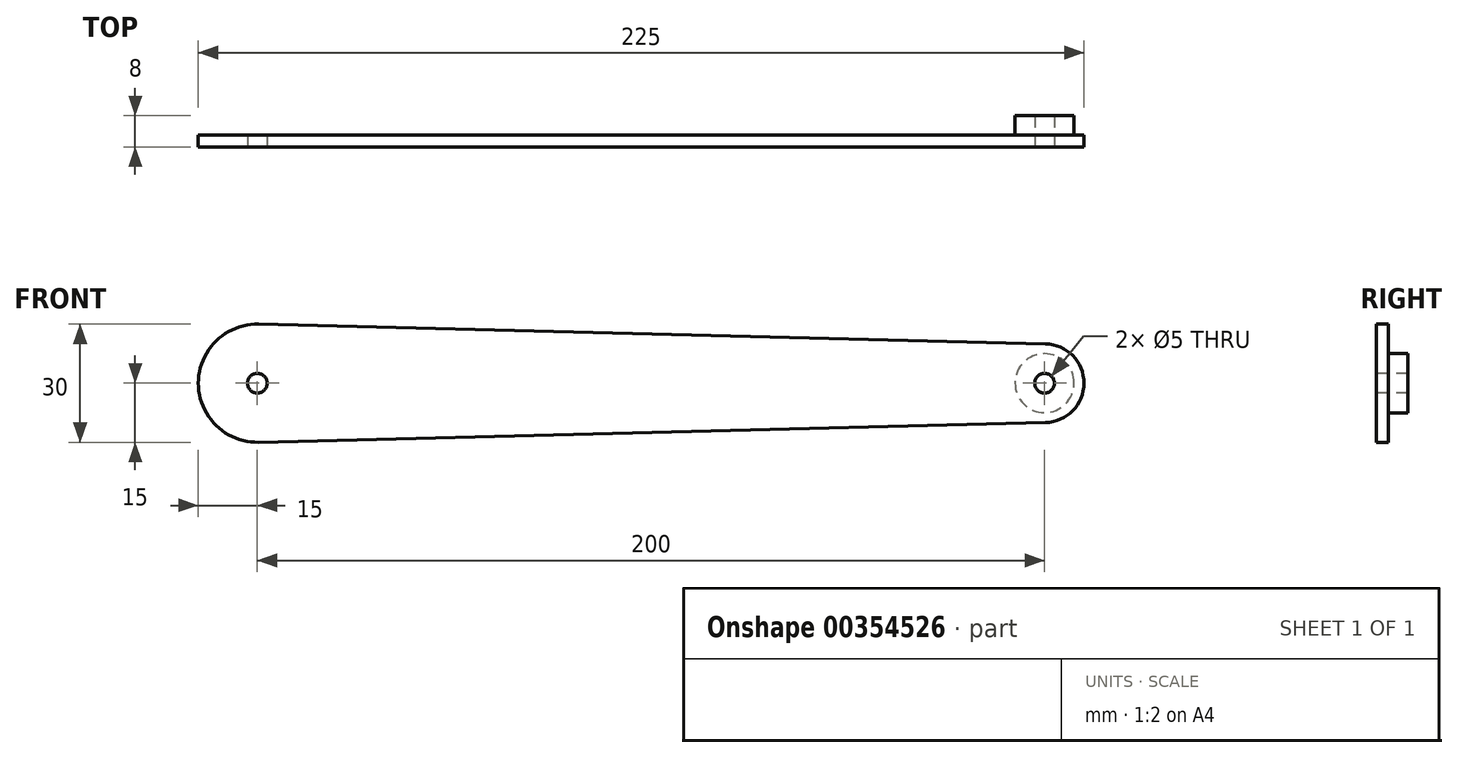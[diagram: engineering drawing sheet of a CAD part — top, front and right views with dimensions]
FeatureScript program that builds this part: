
annotation { "Feature Type Name" : "Feature", "Feature Type Description" : "" }
export const myFeature = defineFeature(function(context is Context, id is Id, definition is map)
    precondition{}
    {
        {
            var Q0;
            Q0=qCreatedBy(makeId("Front.planeOp"),FACE);
            var sketch = newSketch(context, id + "F0", { "sketchPlane" : qUnion([Q0])});
            skArc(sketch, "E0", {"start": v(0.38, 15) * mm, "mid": v(-15, 0) * mm, "end": v(0.37, -15) * mm});
            skArc(sketch, "E1", {"start": v(200.25, 10) * mm, "mid": v(210, 0) * mm, "end": v(200.25, -10) * mm});
            skLineSegment(sketch, "E2", {"start": v(0.37, 15) * mm, "end": v(200.25, 10) * mm});
            skLineSegment(sketch, "E3", {"start": v(200.25, -10) * mm, "end": v(0.37, -15) * mm});
            skCircle(sketch, "E4", {"center": v(200, 0) * mm, "radius": 2.5 * mm});
            skSolve(sketch);
        }
        {
            var Q0;
            Q0 = qSketchRegion(id + "F0", true);
            extrude(context, id + "F1", {"entities" : qUnion([Q0]), "oppositeDirection" : true, "depth" : 3 * mm});
        }
        {
            var Q0;
            Q0=makeQuery(id+"F1.opExtrude","CAP_FACE",FACE,{"disambiguationData":[OSD([sQuery(id+"F0.wireOp",EDGE,"E0"),sQuery(id+"F0.wireOp",EDGE,"E1"),sQuery(id+"F0.wireOp",EDGE,"E2"),sQuery(id+"F0.wireOp",EDGE,"E3"),sQuery(id+"F0.wireOp",EDGE,"1bxTtMlZ-ZWaT-lLSa-SvVQ-4AnmRSgOc4nz"),sQuery(id+"F0.wireOp",EDGE,"E4")])],"isStart":true});
            var sketch = newSketch(context, id + "F2", { "sketchPlane" : qUnion([Q0])});
            skCircle(sketch, "E5", {"center": v(0, 0) * mm, "radius": 2.5 * mm});
            skSolve(sketch);
        }
        {
            var Q0;
            Q0=makeQuery(id+"F2.imprint","IMPRINT",FACE,{"disambiguationData":[TD([[makeQuery(id+"F2.imprint","IMPRINT",EDGE,{"derivedFrom":sQuery(id+"F2.wireOp",EDGE,"RoWl6hh7-x6r5-yKus-qSID-FwlCdr2q77XN")}),1.0]])]});
            var Q1;
            Q1=makeQuery(id+"F2.imprint","IMPRINT",FACE,{"disambiguationData":[TD([[makeQuery(id+"F2.imprint","IMPRINT",EDGE,{"derivedFrom":sQuery(id+"F2.wireOp",EDGE,"E5")}),1.0]])]});
            extrude(context, id + "F3", {"entities" : qUnion([Q0, Q1]), "depth" : 25 * mm, "offsetDistance" : 25 * mm});
        }
        {
            var Q0;
            Q0=makeQuery(id+"F1.opExtrude","CAP_FACE",FACE,{"disambiguationData":[OSD([sQuery(id+"F0.wireOp",EDGE,"E0"),sQuery(id+"F0.wireOp",EDGE,"E1"),sQuery(id+"F0.wireOp",EDGE,"E2"),sQuery(id+"F0.wireOp",EDGE,"E3"),sQuery(id+"F0.wireOp",EDGE,"E4")])],"isStart":false});
            var sketch = newSketch(context, id + "F4", { "sketchPlane" : qUnion([Q0])});
            skCircle(sketch, "E6", {"center": v(-200, 0) * mm, "radius": 7.5 * mm});
            skSolve(sketch);
        }
        {
            var Q0;
            Q0=makeQuery(id+"F4.imprint","IMPRINT",FACE,{"disambiguationData":[TD([[makeQuery(id+"F4.imprint","IMPRINT",EDGE,{"derivedFrom":sQuery(id+"F4.wireOp",EDGE,"E6")}),1.0]])]});
            extrude(context, id + "F5", {"entities" : qUnion([Q0]), "operationType" : NewBodyOperationType.ADD, "depth" : 5 * mm, "offsetDistance" : 25 * mm});
        }
        {
            var Q0;
            Q0=makeQuery(id+"F3.opExtrude","SWEPT_BODY",BODY,{"disambiguationData":[OSD([sQuery(id+"F2.wireOp",EDGE,"E5")])]});
            deleteBodies(context, id + "F6", {"entities" : qUnion([Q0])});
        }
        {
            var Q0;
            Q0 = qSketchRegion(id + "F2", true);
            extrude(context, id + "F7", {"entities" : qUnion([Q0]), "operationType" : NewBodyOperationType.REMOVE, "endBound" : BoundingType.UP_TO_NEXT, "oppositeDirection" : true, "depth" : 25 * mm, "offsetDistance" : 25 * mm});
        }
    });
